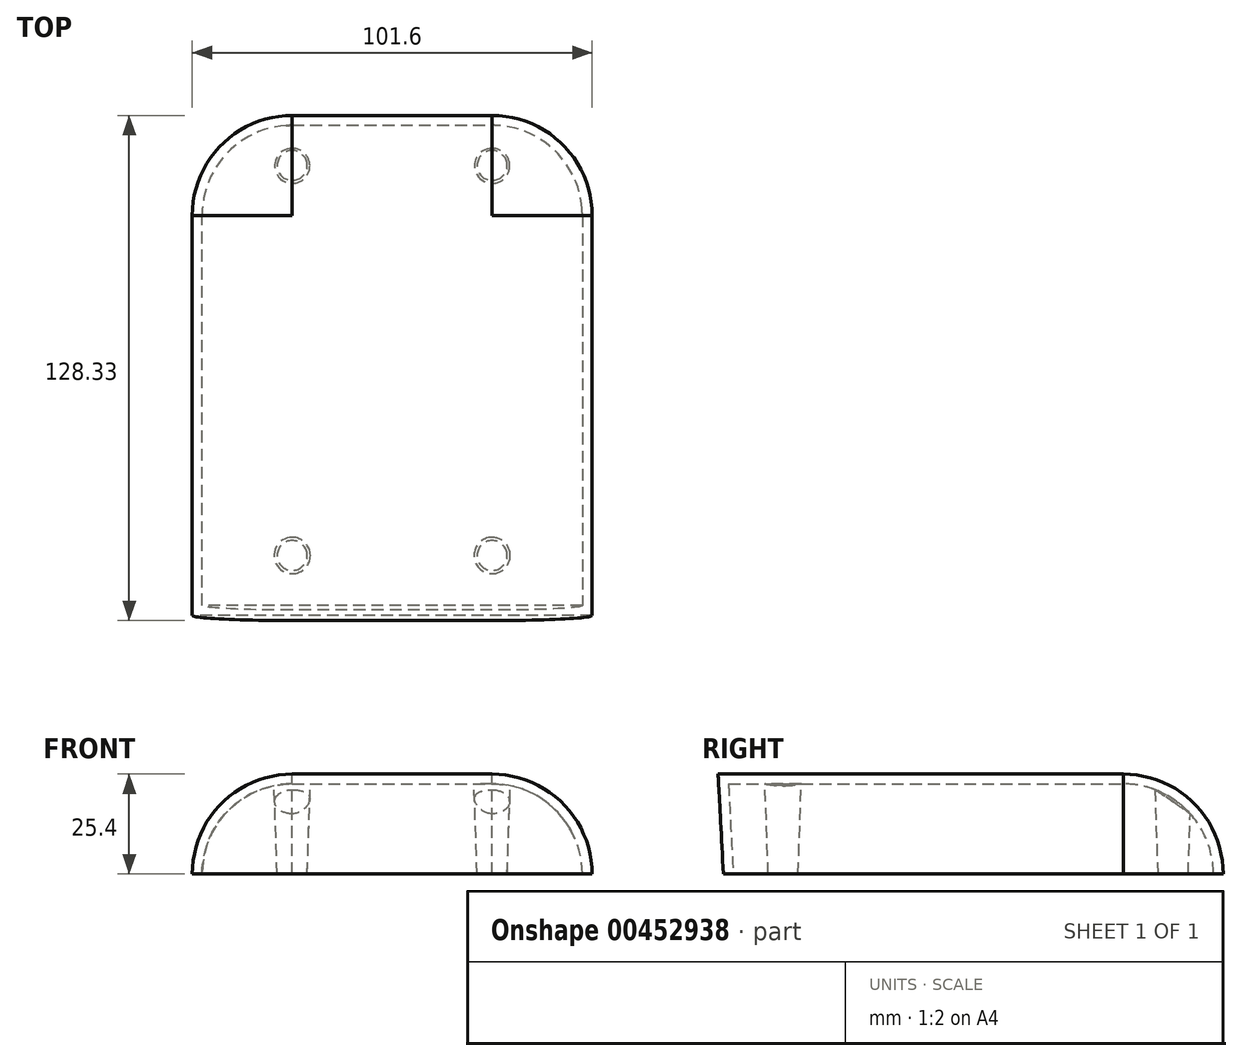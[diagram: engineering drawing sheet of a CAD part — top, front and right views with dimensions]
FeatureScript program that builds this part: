
annotation { "Feature Type Name" : "Feature", "Feature Type Description" : "" }
export const myFeature = defineFeature(function(context is Context, id is Id, definition is map)
    precondition{}
    {
        {
            var Q0;
            Q0=qCreatedBy(makeId("Top.planeOp"),FACE);
            var sketch = newSketch(context, id + "F0", { "sketchPlane" : qUnion([Q0])});
            skLineSegment(sketch, "E0.bottom", {"start": v(25.4, 63.5) * mm, "end": v(-25.4, 63.5) * mm});
            skLineSegment(sketch, "E0.top", {"start": v(50.8, -63.5) * mm, "end": v(-50.8, -63.5) * mm});
            skLineSegment(sketch, "E0.left", {"start": v(50.8, 38.1) * mm, "end": v(50.8, -63.5) * mm});
            skLineSegment(sketch, "E0.right", {"start": v(-50.8, 38.1) * mm, "end": v(-50.8, -63.5) * mm});
            skPoint(sketch, "E0.middle", {"position": v(0, 0) * mm});
            skArc(sketch, "E1", {"start": v(-25.4, 63.5) * mm, "mid": v(-43.36, 56.06) * mm, "end": v(-50.8, 38.1) * mm});
            skArc(sketch, "E2", {"start": v(50.8, 38.1) * mm, "mid": v(43.36, 56.06) * mm, "end": v(25.4, 63.5) * mm});
            skPoint(sketch, "E3.orphan", {"position": v(50.8, 63.5) * mm});
            skPoint(sketch, "E4.orphan", {"position": v(-50.8, 63.5) * mm});
            skSolve(sketch);
        }
        {
            var Q0;
            Q0 = qSketchRegion(id + "F0", true);
            extrude(context, id + "F1", {"entities" : qUnion([Q0]), "depth" : 25.4 * mm, "hasDraft" : true, "draftAngle" : 3 * degree});
        }
        {
            var Q0;
            Q0=makeQuery(id+"F1.opExtrude","CAP_EDGE",EDGE,{"disambiguationData":[OSD([sQuery(id+"F0.wireOp",EDGE,"E1")])],"isStart":false});
            fillet(context, id + "F2", {"entities" : qUnion([Q0]), "radius" : 25.4 * mm, "tangentPropagation" : true, "allowEdgeOverflow" : false});
        }
        {
            var Q0;
            Q0=makeQuery(id+"F1.opExtrude","CAP_FACE",FACE,{"disambiguationData":[OSD([sQuery(id+"F0.wireOp",EDGE,"E0.bottom"),sQuery(id+"F0.wireOp",EDGE,"E0.top"),sQuery(id+"F0.wireOp",EDGE,"E0.left"),sQuery(id+"F0.wireOp",EDGE,"E0.right"),sQuery(id+"F0.wireOp",EDGE,"E1"),sQuery(id+"F0.wireOp",EDGE,"E2")])],"isStart":true});
            shell(context, id + "F3", {"entities" : qUnion([Q0]), "thickness" : 2.5 * mm});
        }
        {
            var Q0;
            Q0=qCreatedBy(makeId("Top.planeOp"),FACE);
            var sketch = newSketch(context, id + "F4", { "sketchPlane" : qUnion([Q0])});
            skCircle(sketch, "E5", {"center": v(25.4, 50.8) * mm, "radius": 3.81 * mm});
            skCircle(sketch, "E6", {"center": v(-25.4, 50.8) * mm, "radius": 3.81 * mm});
            skCircle(sketch, "E7", {"center": v(25.4, -48.3) * mm, "radius": 3.81 * mm});
            skCircle(sketch, "E8", {"center": v(-25.4, -48.3) * mm, "radius": 3.81 * mm});
            skLineSegment(sketch, "E9", {"start": v(25.4, 50.8) * mm, "end": v(-25.4, 50.8) * mm, "construction": true});
            skLineSegment(sketch, "E10", {"start": v(25.4, 50.8) * mm, "end": v(25.4, -48.3) * mm, "construction": true});
            skLineSegment(sketch, "E11", {"start": v(-25.4, -48.3) * mm, "end": v(25.4, -48.3) * mm, "construction": true});
            skLineSegment(sketch, "E12", {"start": v(-25.4, -48.3) * mm, "end": v(-25.4, 50.8) * mm, "construction": true});
            skSolve(sketch);
        }
        {
            var Q0;
            Q0 = qSketchRegion(id + "F4", true);
            var Q1;
            Q1=makeQuery(id+"F1.opExtrude","SWEPT_BODY",BODY,{"disambiguationData":[OSD([sQuery(id+"F0.wireOp",EDGE,"E0.bottom"),sQuery(id+"F0.wireOp",EDGE,"E0.top"),sQuery(id+"F0.wireOp",EDGE,"E0.left"),sQuery(id+"F0.wireOp",EDGE,"E0.right"),sQuery(id+"F0.wireOp",EDGE,"E1"),sQuery(id+"F0.wireOp",EDGE,"E2")])]});
            extrude(context, id + "F5", {"entities" : qUnion([Q0]), "operationType" : NewBodyOperationType.ADD, "endBound" : BoundingType.UP_TO_BODY, "endBoundEntityBody" : qUnion([Q1]), "depth" : 25.4 * mm, "hasDraft" : true, "draftAngle" : 2 * degree});
        }
    });
